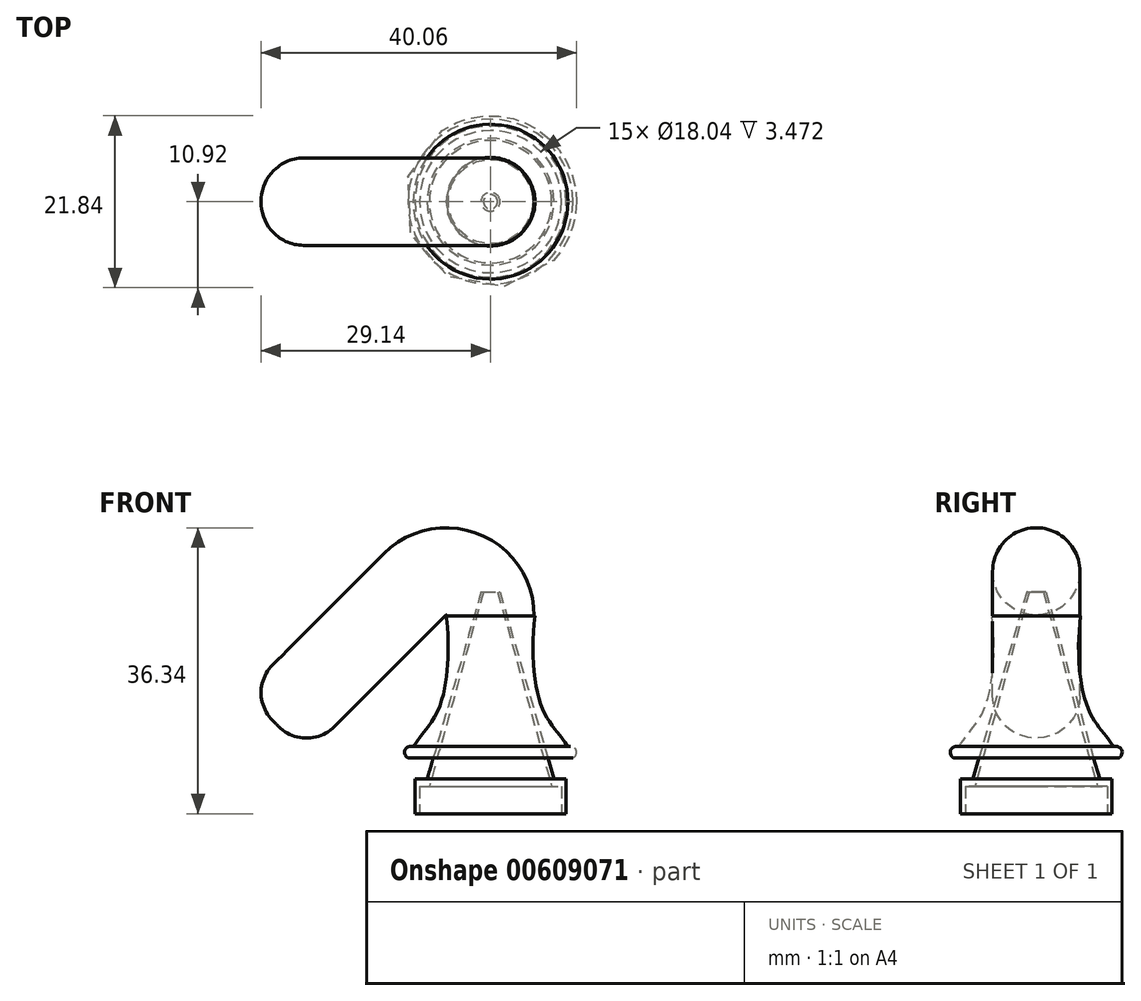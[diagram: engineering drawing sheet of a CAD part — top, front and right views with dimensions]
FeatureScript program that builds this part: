
annotation { "Feature Type Name" : "Feature", "Feature Type Description" : "" }
export const myFeature = defineFeature(function(context is Context, id is Id, definition is map)
    precondition{}
    {
        {
            var Q0;
            Q0=qCreatedBy(makeId("Front.planeOp"),FACE);
            var sketch = newSketch(context, id + "F0", { "sketchPlane" : qUnion([Q0])});
            skFitSpline(sketch, "E0", {"points": [v(0, 43.5) * mm, v(-4.13, 42.47) * mm, v(-6.3, 36.34) * mm, v(-23.95, 24.8) * mm, v(-31.88, -21.33) * mm, v(-13.86, -40.8) * mm, v(-6.3, -51.24) * mm, v(-6.3, -65.66) * mm, v(-9.18, -70.35) * mm, v(-10.26, -75.4) * mm, v(0, -78.11) * mm, v(0, 43.5) * mm]});
            skLineSegment(sketch, "E1.bottom", {"start": v(0, 51.12) * mm, "end": v(20.74, 51.12) * mm});
            skLineSegment(sketch, "E1.top", {"start": v(0, -82.24) * mm, "end": v(20.74, -82.24) * mm});
            skLineSegment(sketch, "E1.left", {"start": v(0, 51.12) * mm, "end": v(0, -82.24) * mm});
            skLineSegment(sketch, "E1.right", {"start": v(20.74, 51.12) * mm, "end": v(20.74, -82.24) * mm});
            skArc(sketch, "E2", {"start": v(0, 45.4) * mm, "mid": v(-2.55, 44.62) * mm, "end": v(-4.13, 42.47) * mm});
            skLineSegment(sketch, "E3.bottom", {"start": v(6.03, -72.7) * mm, "end": v(-10.95, -72.7) * mm});
            skLineSegment(sketch, "E3.top", {"start": v(6.03, -82.24) * mm, "end": v(-10.95, -82.24) * mm});
            skLineSegment(sketch, "E3.left", {"start": v(6.03, -72.7) * mm, "end": v(6.03, -82.24) * mm});
            skLineSegment(sketch, "E3.right", {"start": v(-10.95, -72.7) * mm, "end": v(-10.95, -82.24) * mm});
            skArc(sketch, "E4", {"start": v(-9.83, -71.3) * mm, "mid": v(-10.85, -71.68) * mm, "end": v(-10.47, -72.7) * mm});
            skLineSegment(sketch, "E5.bottom", {"start": v(0, 51.12) * mm, "end": v(-37.1, 51.12) * mm});
            skLineSegment(sketch, "E5.top", {"start": v(0, -54.64) * mm, "end": v(-37.1, -54.64) * mm});
            skLineSegment(sketch, "E5.left", {"start": v(0, 51.12) * mm, "end": v(0, -54.64) * mm});
            skLineSegment(sketch, "E5.right", {"start": v(-37.1, 51.12) * mm, "end": v(-37.1, -54.64) * mm});
            skSolve(sketch);
        }
        {
            var Q0;
            {var subQ0=sQuery(id+"F0.wireOp",EDGE,"E4");var subQ2=sQuery(id+"F0.wireOp",EDGE,"E0");var subQ8=makeQuery(id+"F0.imprint","INTERSECT",VERTEX,{"derivedFrom":[subQ2,subQ0]});Q0=makeQuery(id+"F0.imprint","IMPRINT",FACE,{"disambiguationData":[TD([[makeQuery(id+"F0.imprint","IMPRINT",EDGE,{"disambiguationData":[TD([[subQ8,1.0]])],"derivedFrom":subQ2}),1.0]])]});}
            var Q1;
            {var subQ0=sQuery(id+"F0.wireOp",EDGE,"E4");Q1=makeQuery(id+"F0.imprint","IMPRINT",FACE,{"disambiguationData":[TD([[makeQuery(id+"F0.imprint","IMPRINT",EDGE,{"derivedFrom":subQ0}),1.0]])]});}
            var Q2;
            Q2=sQuery(id+"F0.wireOp",EDGE,"E1.left");
            revolve(context, id + "F1", {"entities" : qUnion([Q0, Q1]), "axis" : qUnion([Q2]), "revolveType" : RevolveType.FULL});
        }
        {
            var Q0;
            Q0=qCreatedBy(makeId("Front.planeOp"),FACE);
            var sketch = newSketch(context, id + "F2", { "sketchPlane" : qUnion([Q0])});
            skLineSegment(sketch, "E6.bottom", {"start": v(-5.8, -54.63) * mm, "end": v(-7.1, -54.63) * mm});
            skLineSegment(sketch, "E6.top", {"start": v(-5.8, -61) * mm, "end": v(-7.1, -61) * mm});
            skLineSegment(sketch, "E6.left", {"start": v(-5.8, -54.63) * mm, "end": v(-5.8, -61) * mm});
            skLineSegment(sketch, "E6.right", {"start": v(-7.1, -54.63) * mm, "end": v(-7.1, -61) * mm});
            skSolve(sketch);
        }
        {
            var Q0;
            Q0=qCreatedBy(makeId("Right.planeOp"),FACE);
            var sketch = newSketch(context, id + "F3", { "sketchPlane" : qUnion([Q0])});
            skLineSegment(sketch, "E7", {"start": v(0, -51.6) * mm, "end": v(1.2, -51.6) * mm});
            skLineSegment(sketch, "E8", {"start": v(1.2, -51.6) * mm, "end": v(8.05, -75.4) * mm});
            skLineSegment(sketch, "E9", {"start": v(8.05, -75.4) * mm, "end": v(9.6, -75.4) * mm});
            skLineSegment(sketch, "E10", {"start": v(9.6, -75.4) * mm, "end": v(9.6, -79.8) * mm});
            skLineSegment(sketch, "E11", {"start": v(9.6, -79.8) * mm, "end": v(0, -79.8) * mm});
            skLineSegment(sketch, "E12", {"start": v(0, -79.8) * mm, "end": v(0, -51.6) * mm});
            skLineSegment(sketch, "E13", {"start": v(0.9, -51.6) * mm, "end": v(7.78, -76.33) * mm});
            skLineSegment(sketch, "E14", {"start": v(7.78, -76.33) * mm, "end": v(9.02, -76.33) * mm});
            skLineSegment(sketch, "E15", {"start": v(9.02, -76.33) * mm, "end": v(9.02, -79.8) * mm});
            skLineSegment(sketch, "E16", {"start": v(9.02, -79.8) * mm, "end": v(9.6, -79.8) * mm});
            skSolve(sketch);
        }
        {
            var Q0;
            {var subQ0=sQuery(id+"F3.wireOp",EDGE,"E8");Q0=makeQuery(id+"F3.imprint","IMPRINT",FACE,{"disambiguationData":[TD([[makeQuery(id+"F3.imprint","IMPRINT",EDGE,{"derivedFrom":subQ0}),-1.0]])]});}
            var Q1;
            Q1=sQuery(id+"F3.wireOp",EDGE,"E12");
            revolve(context, id + "F4", {"entities" : qUnion([Q0]), "axis" : qUnion([Q1]), "revolveType" : RevolveType.FULL});
        }
        {
            var Q0;
            Q0=makeQuery(id+"F1.opRevolve","SWEPT_FACE",FACE,{"disambiguationData":[OSD([sQuery(id+"F0.wireOp",EDGE,"E5.top")])]});
            var sketch = newSketch(context, id + "F5", { "sketchPlane" : qUnion([Q0])});
            skCircle(sketch, "E17", {"center": v(0, 0) * mm, "radius": 5.55 * mm});
            skLineSegment(sketch, "E18", {"start": v(-5.63, 0) * mm, "end": v(-5.63, 5.17) * mm});
            skSolve(sketch);
        }
        {
            var Q0;
            Q0=makeQuery(id+"F5.imprint","IMPRINT",FACE,{"disambiguationData":[TD([[makeQuery(id+"F5.imprint","IMPRINT",EDGE,{"derivedFrom":sQuery(id+"F5.wireOp",EDGE,"E17")}),1.0]])]});
            var Q1;
            Q1=sQuery(id+"F5.wireOp",EDGE,"E18");
            revolve(context, id + "F6", {"entities" : qUnion([Q0]), "axis" : qUnion([Q1]), "revolveType" : RevolveType.ONE_DIRECTION, "oppositeDirection" : true, "angle" : 135 * degree});
        }
        {
            var Q0;
            Q0=makeQuery(id+"F6.opRevolve","CAP_FACE",FACE,{"disambiguationData":[OSD([sQuery(id+"F5.wireOp",EDGE,"E17")])],"isStart":false});
            extrude(context, id + "F7", {"entities" : qUnion([Q0]), "operationType" : NewBodyOperationType.ADD, "depth" : 25 * mm});
        }
        {
            var Q0;
            Q0=makeQuery(id+"F7.opExtrude","CAP_FACE",FACE,{"disambiguationData":[OSD([sQuery(id+"F5.wireOp",EDGE,"E17")])],"isStart":false});
            fillet(context, id + "F8", {"entities" : qUnion([Q0]), "radius" : 5 * mm, "tangentPropagation" : true, "allowEdgeOverflow" : false});
        }
    });
